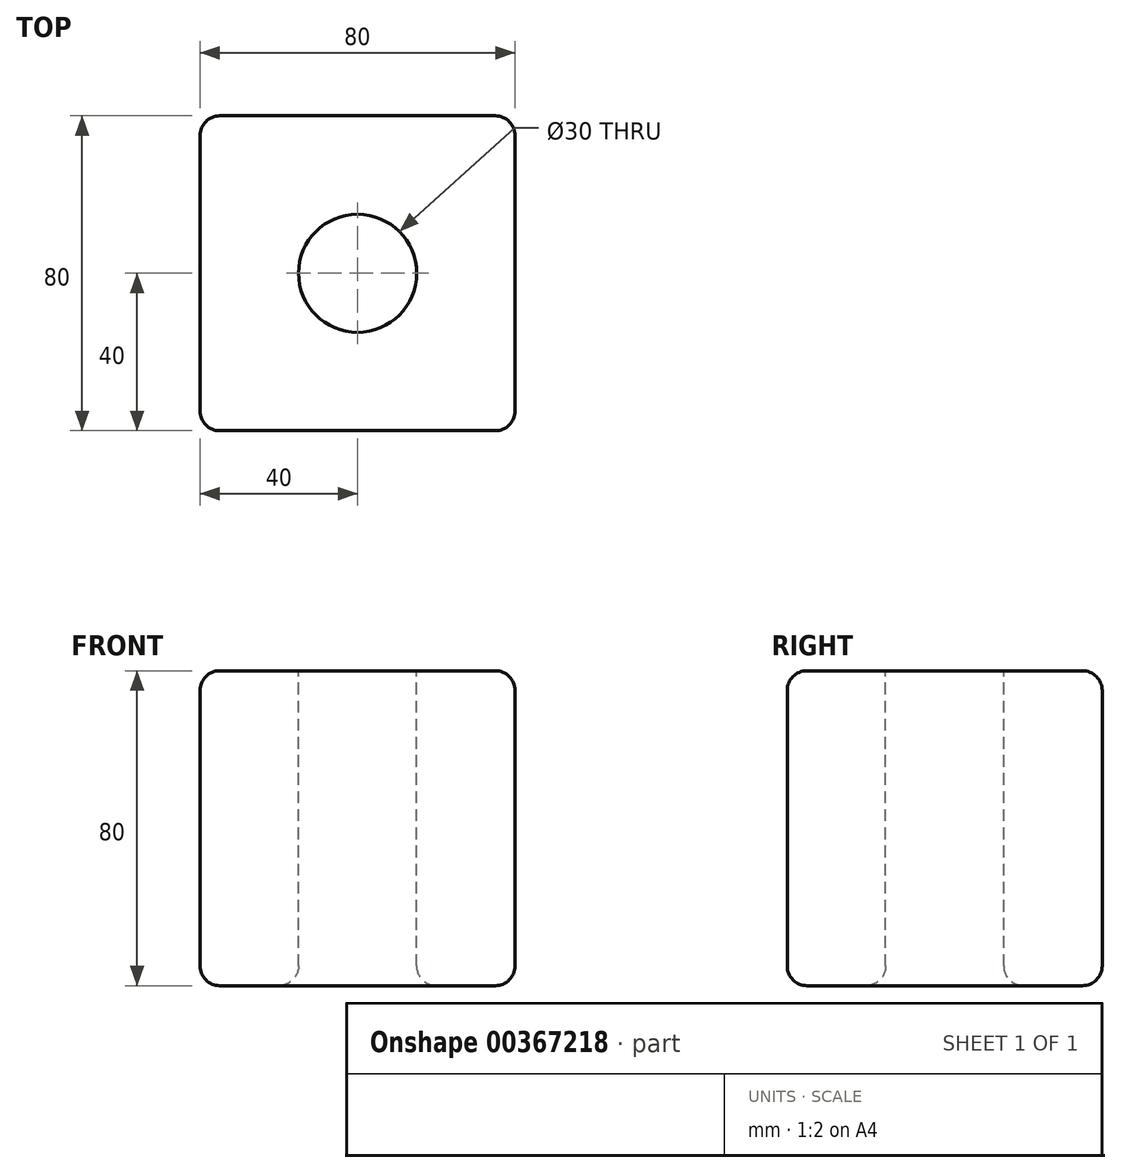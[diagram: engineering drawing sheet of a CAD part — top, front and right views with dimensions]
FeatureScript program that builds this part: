
annotation { "Feature Type Name" : "Feature", "Feature Type Description" : "" }
export const myFeature = defineFeature(function(context is Context, id is Id, definition is map)
    precondition{}
    {
        {
            var Q0;
            Q0=qCreatedBy(makeId("Top.planeOp"),FACE);
            var sketch = newSketch(context, id + "F0", { "sketchPlane" : qUnion([Q0])});
            skLineSegment(sketch, "E0.bottom", {"start": v(-40, 40) * mm, "end": v(40, 40) * mm});
            skLineSegment(sketch, "E0.top", {"start": v(-40, -40) * mm, "end": v(40, -40) * mm});
            skLineSegment(sketch, "E0.left", {"start": v(-40, 40) * mm, "end": v(-40, -40) * mm});
            skLineSegment(sketch, "E0.right", {"start": v(40, 40) * mm, "end": v(40, -40) * mm});
            skPoint(sketch, "E0.middle", {"position": v(0, 0) * mm});
            skSolve(sketch);
        }
        {
            var Q0;
            Q0=makeQuery(id+"F0.imprint","IMPRINT",FACE,{"disambiguationData":[TD([[makeQuery(id+"F0.imprint","IMPRINT",EDGE,{"derivedFrom":sQuery(id+"F0.wireOp",EDGE,"E0.bottom")}),-1.0]])]});
            extrude(context, id + "F1", {"entities" : qUnion([Q0]), "depth" : 80 * mm});
        }
        {
            var Q0;
            Q0=makeQuery(id+"F1.opExtrude","CAP_FACE",FACE,{"disambiguationData":[OSD([sQuery(id+"F0.wireOp",EDGE,"E0.bottom"),sQuery(id+"F0.wireOp",EDGE,"E0.top"),sQuery(id+"F0.wireOp",EDGE,"E0.left"),sQuery(id+"F0.wireOp",EDGE,"E0.right")])],"isStart":false});
            var sketch = newSketch(context, id + "F2", { "sketchPlane" : qUnion([Q0])});
            skCircle(sketch, "E1", {"center": v(0, 0) * mm, "radius": 15 * mm});
            skSolve(sketch);
        }
        {
            var Q0;
            Q0=makeQuery(id+"F2.imprint","IMPRINT",FACE,{"disambiguationData":[TD([[makeQuery(id+"F2.imprint","IMPRINT",EDGE,{"derivedFrom":sQuery(id+"F2.wireOp",EDGE,"E1")}),1.0]])]});
            extrude(context, id + "F3", {"entities" : qUnion([Q0]), "operationType" : NewBodyOperationType.REMOVE, "endBound" : BoundingType.THROUGH_ALL, "oppositeDirection" : true, "depth" : 25 * mm});
        }
        {
            var Q0;
            Q0=makeQuery(id+"F1.opExtrude","CAP_EDGE",EDGE,{"disambiguationData":[OSD([sQuery(id+"F0.wireOp",EDGE,"E0.bottom")])],"isStart":false});
            var Q1;
            Q1=makeQuery(id+"F1.opExtrude","CAP_EDGE",EDGE,{"disambiguationData":[OSD([sQuery(id+"F0.wireOp",EDGE,"E0.left")])],"isStart":false});
            var Q2;
            Q2=makeQuery(id+"F1.opExtrude","CAP_EDGE",EDGE,{"disambiguationData":[OSD([sQuery(id+"F0.wireOp",EDGE,"E0.top")])],"isStart":false});
            var Q3;
            Q3=makeQuery(id+"F1.opExtrude","CAP_EDGE",EDGE,{"disambiguationData":[OSD([sQuery(id+"F0.wireOp",EDGE,"E0.right")])],"isStart":false});
            var Q4;
            Q4=makeQuery(id+"F1.opExtrude","SWEPT_EDGE",EDGE,{"disambiguationData":[OSD([sQuery(id+"F0.wireOp",EDGE,"E0.top"),sQuery(id+"F0.wireOp",EDGE,"E0.left")])]});
            var Q5;
            Q5=makeQuery(id+"F1.opExtrude","SWEPT_EDGE",EDGE,{"disambiguationData":[OSD([sQuery(id+"F0.wireOp",EDGE,"E0.top"),sQuery(id+"F0.wireOp",EDGE,"E0.right")])]});
            var Q6;
            Q6=makeQuery(id+"F1.opExtrude","SWEPT_FACE",FACE,{"disambiguationData":[OSD([sQuery(id+"F0.wireOp",EDGE,"E0.top")])]});
            var Q7;
            Q7=makeQuery(id+"F1.opExtrude","CAP_EDGE",EDGE,{"disambiguationData":[OSD([sQuery(id+"F0.wireOp",EDGE,"E0.top")])],"isStart":true});
            var Q8;
            Q8=makeQuery(id+"F1.opExtrude","CAP_EDGE",EDGE,{"disambiguationData":[OSD([sQuery(id+"F0.wireOp",EDGE,"E0.left")])],"isStart":true});
            var Q9;
            Q9=makeQuery(id+"F1.opExtrude","SWEPT_EDGE",EDGE,{"disambiguationData":[OSD([sQuery(id+"F0.wireOp",EDGE,"E0.bottom"),sQuery(id+"F0.wireOp",EDGE,"E0.left")])]});
            var Q10;
            Q10=makeQuery(id+"F3.boolean.opBoolean","COPY",EDGE,{"derivedFrom":makeQuery(id+"F3.opExtrude","CAP_EDGE",EDGE,{"disambiguationData":[OSD([sQuery(id+"F2.wireOp",EDGE,"E1")])],"isStart":true})});
            var Q11;
            Q11=makeQuery(id+"F1.opExtrude","CAP_EDGE",EDGE,{"disambiguationData":[OSD([sQuery(id+"F0.wireOp",EDGE,"E0.right")])],"isStart":true});
            var Q12;
            Q12=makeQuery(id+"F3.boolean.opBoolean","INTERSECT",EDGE,{"derivedFrom":[makeQuery(id+"F1.opExtrude","CAP_FACE",FACE,{"disambiguationData":[OSD([sQuery(id+"F0.wireOp",EDGE,"E0.bottom"),sQuery(id+"F0.wireOp",EDGE,"E0.top"),sQuery(id+"F0.wireOp",EDGE,"E0.left"),sQuery(id+"F0.wireOp",EDGE,"E0.right")])],"isStart":true}),makeQuery(id+"F3.opExtrude","SWEPT_FACE",FACE,{"disambiguationData":[OSD([sQuery(id+"F2.wireOp",EDGE,"E1")])]})]});
            var Q13;
            Q13=makeQuery(id+"F1.opExtrude","CAP_FACE",FACE,{"disambiguationData":[OSD([sQuery(id+"F0.wireOp",EDGE,"E0.bottom"),sQuery(id+"F0.wireOp",EDGE,"E0.top"),sQuery(id+"F0.wireOp",EDGE,"E0.left"),sQuery(id+"F0.wireOp",EDGE,"E0.right")])],"isStart":true});
            var Q14;
            Q14=makeQuery(id+"F1.opExtrude","SWEPT_EDGE",EDGE,{"disambiguationData":[OSD([sQuery(id+"F0.wireOp",EDGE,"E0.bottom"),sQuery(id+"F0.wireOp",EDGE,"E0.right")])]});
            fillet(context, id + "F4", {"entities" : qUnion([Q0, Q1, Q2, Q3, Q4, Q5, Q6, Q7, Q8, Q9, Q10, Q11, Q12, Q13, Q14]), "radius" : 5 * mm, "tangentPropagation" : true, "allowEdgeOverflow" : false});
        }
    });
